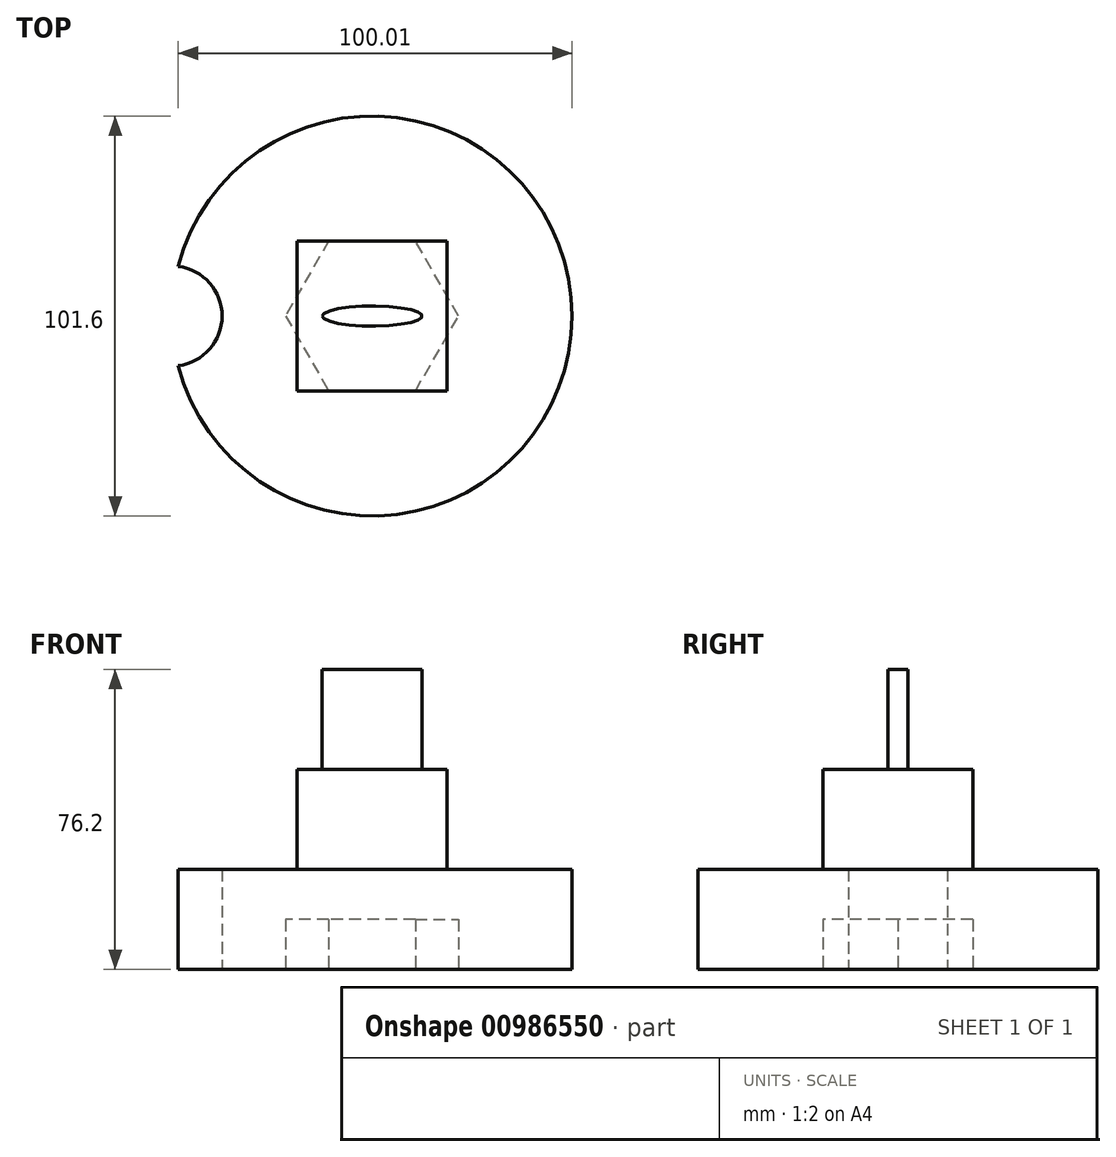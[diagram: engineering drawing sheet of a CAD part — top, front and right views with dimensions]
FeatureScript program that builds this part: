
annotation { "Feature Type Name" : "Feature", "Feature Type Description" : "" }
export const myFeature = defineFeature(function(context is Context, id is Id, definition is map)
    precondition{}
    {
        {
            var Q0;
            Q0=qCreatedBy(makeId("Top.planeOp"),FACE);
            var sketch = newSketch(context, id + "F0", { "sketchPlane" : qUnion([Q0])});
            skArc(sketch, "E0", {"start": v(-49.21, -12.6) * mm, "mid": v(50.8, 0) * mm, "end": v(-49.21, 12.6) * mm});
            skArc(sketch, "E1", {"start": v(-49.21, -12.6) * mm, "mid": v(-38.1, 0) * mm, "end": v(-49.21, 12.6) * mm});
            skSolve(sketch);
        }
        {
            var Q0;
            Q0 = qSketchRegion(id + "F0", false);
            extrude(context, id + "F1", {"entities" : qUnion([Q0]), "depth" : 25.4 * mm});
        }
        {
            var Q0;
            Q0=makeQuery(id+"F1.opExtrude","CAP_FACE",FACE,{"disambiguationData":[OSD([sQuery(id+"F0.wireOp",EDGE,"E0"),sQuery(id+"F0.wireOp",EDGE,"E1")])],"isStart":false});
            var sketch = newSketch(context, id + "F2", { "sketchPlane" : qUnion([Q0])});
            skLineSegment(sketch, "E2", {"start": v(-19.05, 19.05) * mm, "end": v(19.05, 19.05) * mm});
            skLineSegment(sketch, "E3", {"start": v(-19.05, 19.05) * mm, "end": v(-19.05, -19.05) * mm});
            skLineSegment(sketch, "E4", {"start": v(-19.05, -19.05) * mm, "end": v(19.05, -19.05) * mm});
            skLineSegment(sketch, "E5", {"start": v(19.05, 19.05) * mm, "end": v(19.05, -19.05) * mm});
            skLineSegment(sketch, "E6", {"start": v(-19.05, 19.05) * mm, "end": v(19.05, -19.05) * mm});
            skLineSegment(sketch, "E7", {"start": v(-19.05, -19.05) * mm, "end": v(19.05, 19.05) * mm});
            skPoint(sketch, "E8", {"position": v(0, 0) * mm});
            skSolve(sketch);
        }
        {
            var Q0;
            Q0 = qSketchRegion(id + "F2", false);
            extrude(context, id + "F3", {"entities" : qUnion([Q0]), "operationType" : NewBodyOperationType.ADD, "depth" : 25.4 * mm});
        }
        {
            var Q0;
            Q0=makeQuery(id+"F3.opExtrude","CAP_FACE",FACE,{"disambiguationData":[OSD([sQuery(id+"F2.wireOp",EDGE,"E2"),sQuery(id+"F2.wireOp",EDGE,"E3"),sQuery(id+"F2.wireOp",EDGE,"E4"),sQuery(id+"F2.wireOp",EDGE,"E5")])],"isStart":false});
            var sketch = newSketch(context, id + "F4", { "sketchPlane" : qUnion([Q0])});
            skEllipse(sketch, "E9", {"center": v(0, 0) * mm, "majorRadius": 12.7 * mm, "minorRadius": 2.54 * mm, "majorAxis": v(-1, 0)});
            skSolve(sketch);
        }
        {
            var Q0;
            Q0 = qSketchRegion(id + "F4", false);
            extrude(context, id + "F5", {"entities" : qUnion([Q0]), "operationType" : NewBodyOperationType.ADD, "depth" : 25.4 * mm});
        }
        {
            var Q0;
            Q0=qCreatedBy(makeId("Top.planeOp"),FACE);
            var sketch = newSketch(context, id + "F6", { "sketchPlane" : qUnion([Q0])});
            skCircle(sketch, "E10", {"center": v(0, 0) * mm, "radius": 19.05 * mm});
            skLineSegment(sketch, "E11", {"start": v(11, 19.05) * mm, "end": v(-11, 19.05) * mm});
            skLineSegment(sketch, "E12", {"start": v(-11, 19.05) * mm, "end": v(-22, 0) * mm});
            skLineSegment(sketch, "E13", {"start": v(-22, 0) * mm, "end": v(-11, -19.05) * mm});
            skLineSegment(sketch, "E14", {"start": v(-11, -19.05) * mm, "end": v(11, -19.05) * mm});
            skLineSegment(sketch, "E15", {"start": v(11, -19.05) * mm, "end": v(22, 0) * mm});
            skLineSegment(sketch, "E16", {"start": v(22, 0) * mm, "end": v(11, 19.05) * mm});
            skSolve(sketch);
        }
        {
            var Q0;
            Q0 = qSketchRegion(id + "F6", false);
            extrude(context, id + "F7", {"entities" : qUnion([Q0]), "operationType" : NewBodyOperationType.REMOVE, "depth" : 12.7 * mm});
        }
    });
